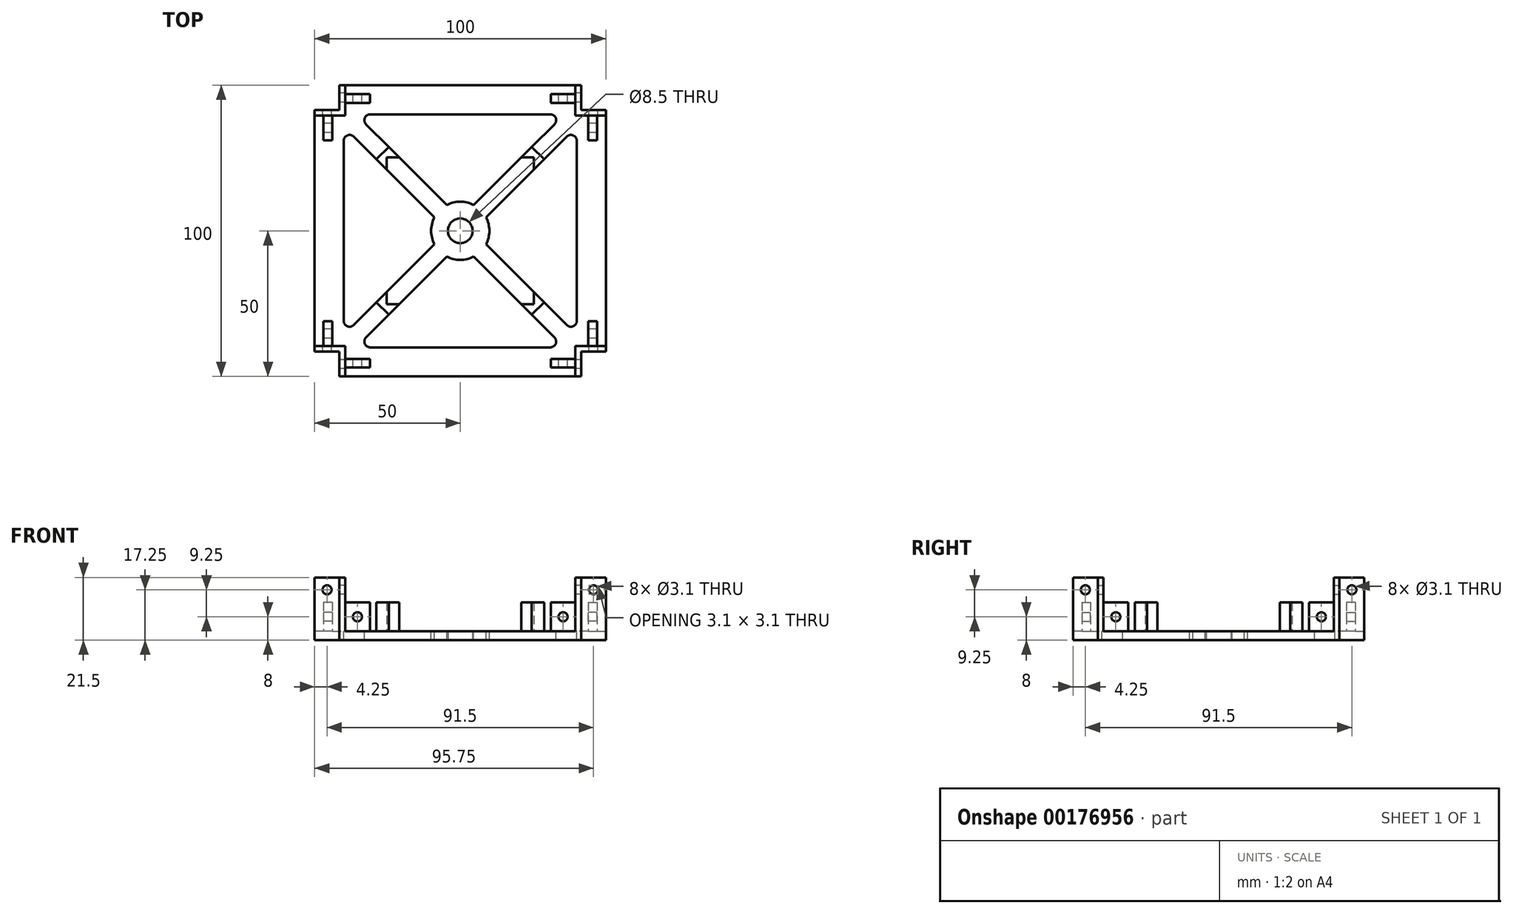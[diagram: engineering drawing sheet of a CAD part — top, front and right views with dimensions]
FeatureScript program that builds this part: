
annotation { "Feature Type Name" : "Feature", "Feature Type Description" : "" }
export const myFeature = defineFeature(function(context is Context, id is Id, definition is map)
    precondition{}
    {
        {
            assignVariable(context, id + "F0", {"name" : "thickness", "anyValue" : 3});
        }
        {
            var Q0;
            Q0=qCreatedBy(makeId("Top.planeOp"),FACE);
            var sketch = newSketch(context, id + "F1", { "sketchPlane" : qUnion([Q0])});
            skLineSegment(sketch, "E0.bottom", {"start": v(41.5, 50) * mm, "end": v(-41.5, 50) * mm});
            skLineSegment(sketch, "E0.top", {"start": v(41.5, -50) * mm, "end": v(-41.5, -50) * mm});
            skLineSegment(sketch, "E0.right", {"start": v(-50, 41.5) * mm, "end": v(-50, -41.5) * mm});
            skPoint(sketch, "E0.middle", {"position": v(0, 0) * mm});
            skLineSegment(sketch, "E1", {"start": v(-50, 41.5) * mm, "end": v(-41.5, 41.5) * mm});
            skLineSegment(sketch, "E2", {"start": v(-41.5, 41.5) * mm, "end": v(-41.5, 50) * mm});
            skLineSegment(sketch, "E3", {"start": v(0, 0) * mm, "end": v(0, 50) * mm, "construction": true});
            skLineSegment(sketch, "E4", {"start": v(0, 0) * mm, "end": v(50, 0) * mm, "construction": true});
            skLineSegment(sketch, "E5.MirrorCS", {"start": v(41.5, 41.5) * mm, "end": v(41.5, 50) * mm});
            skLineSegment(sketch, "E6.MirrorCS", {"start": v(50, 41.5) * mm, "end": v(41.5, 41.5) * mm});
            skLineSegment(sketch, "E7.MirrorCS", {"start": v(-50, -41.5) * mm, "end": v(-41.5, -41.5) * mm});
            skLineSegment(sketch, "E8.MirrorCS", {"start": v(-41.5, -41.5) * mm, "end": v(-41.5, -50) * mm});
            skLineSegment(sketch, "E9.MirrorCS", {"start": v(50, -41.5) * mm, "end": v(41.5, -41.5) * mm});
            skLineSegment(sketch, "E10.MirrorCS", {"start": v(50, -41.5) * mm, "end": v(50, 41.5) * mm});
            skLineSegment(sketch, "E11.MirrorCS", {"start": v(41.5, -41.5) * mm, "end": v(41.5, -50) * mm});
            skCircle(sketch, "E12", {"center": v(0, 0) * mm, "radius": 4.25 * mm});
            skSolve(sketch);
        }
        {
            var Q0;
            Q0=makeQuery(id+"F1.imprint","IMPRINT",FACE,{"disambiguationData":[TD([[makeQuery(id+"F1.imprint","IMPRINT",EDGE,{"derivedFrom":sQuery(id+"F1.wireOp",EDGE,"E0.bottom")}),1.0]])]});
            extrude(context, id + "F2", {"entities" : qUnion([Q0]), "depth" : (getVariable(context, 'thickness')) * mm});
        }
        {
            var Q0;
            Q0=makeQuery(id+"F2.opExtrude","CAP_FACE",FACE,{"disambiguationData":[OSD([sQuery(id+"F1.wireOp",EDGE,"E0.bottom"),sQuery(id+"F1.wireOp",EDGE,"E0.right"),sQuery(id+"F1.wireOp",EDGE,"E1"),sQuery(id+"F1.wireOp",EDGE,"E2"),sQuery(id+"F1.wireOp",EDGE,"E5.MirrorCS"),sQuery(id+"F1.wireOp",EDGE,"E6.MirrorCS"),sQuery(id+"F1.wireOp",EDGE,"E7.MirrorCS"),sQuery(id+"F1.wireOp",EDGE,"E8.MirrorCS"),sQuery(id+"F1.wireOp",EDGE,"E9.MirrorCS"),sQuery(id+"F1.wireOp",EDGE,"E10.MirrorCS"),sQuery(id+"F1.wireOp",EDGE,"E11.MirrorCS"),sQuery(id+"F1.wireOp",EDGE,"E0.top"),sQuery(id+"F1.wireOp",EDGE,"E12")])],"isStart":false});
            var sketch = newSketch(context, id + "F3", { "sketchPlane" : qUnion([Q0])});
            skLineSegment(sketch, "E13", {"start": v(39.55, 43.95) * mm, "end": v(39.55, 39.55) * mm});
            skLineSegment(sketch, "E14", {"start": v(50, 41.5) * mm, "end": v(41.5, 41.5) * mm});
            skLineSegment(sketch, "E15", {"start": v(41.5, 41.5) * mm, "end": v(41.5, 50) * mm});
            skLineSegment(sketch, "E16", {"start": v(39.55, 46.95) * mm, "end": v(31.05, 46.95) * mm});
            skLineSegment(sketch, "E17", {"start": v(0, 0) * mm, "end": v(0, 50) * mm, "construction": true});
            skLineSegment(sketch, "E18", {"start": v(0, 0) * mm, "end": v(50, 0) * mm, "construction": true});
            skLineSegment(sketch, "E19", {"start": v(31.05, 46.95) * mm, "end": v(31.05, 43.95) * mm});
            skLineSegment(sketch, "E20", {"start": v(31.05, 43.95) * mm, "end": v(39.55, 43.95) * mm});
            skLineSegment(sketch, "E21.0", {"start": v(46.95, 39.55) * mm, "end": v(46.95, 31.05) * mm});
            skLineSegment(sketch, "E22", {"start": v(43.95, 31.05) * mm, "end": v(46.95, 31.05) * mm});
            skLineSegment(sketch, "E23.trimOffspring", {"start": v(46.95, 39.55) * mm, "end": v(50, 39.55) * mm});
            skLineSegment(sketch, "E24", {"start": v(39.55, 46.95) * mm, "end": v(39.55, 50) * mm});
            skLineSegment(sketch, "E25", {"start": v(39.55, 50) * mm, "end": v(41.5, 50) * mm});
            skLineSegment(sketch, "E26", {"start": v(43.95, 39.55) * mm, "end": v(39.55, 39.55) * mm});
            skLineSegment(sketch, "E27.trimOffspring", {"start": v(43.95, 39.55) * mm, "end": v(43.95, 31.05) * mm});
            skLineSegment(sketch, "E28", {"start": v(50, 41.5) * mm, "end": v(50, 39.55) * mm});
            skSolve(sketch);
        }
        {
            var Q0;
            Q0=qSketchRegion(id+"F3",true);
            extrude(context, id + "F4", {"entities" : qUnion([Q0]), "depth" : 10 * mm});
        }
        {
            var Q0;
            Q0=makeQuery(id+"F4.opExtrude","SWEPT_BODY",BODY,{"disambiguationData":[OSD([sQuery(id+"F3.wireOp",EDGE,"E13"),sQuery(id+"F3.wireOp",EDGE,"nKXGrhFW-WUnw-J8YZ-HHNa-CiBs2QdvG3Ug"),sQuery(id+"F3.wireOp",EDGE,"9BF3yCzr-lQTs-itfY-5ALy-uFZCs8Egl8vE"),sQuery(id+"F3.wireOp",EDGE,"E14"),sQuery(id+"F3.wireOp",EDGE,"E15"),sQuery(id+"F3.wireOp",EDGE,"E16")])]});
            var Q1;
            Q1=qCreatedBy(makeId("Right.planeOp"),FACE);
            mirror(context, id + "F5", {"entities" : qUnion([Q0]), "mirrorPlane" : qUnion([Q1])});
        }
        {
            var Q0;
            Q0=makeQuery(id+"F5.opPattern","COPY",BODY,{"derivedFrom":makeQuery(id+"F4.opExtrude","SWEPT_BODY",BODY,{"disambiguationData":[OSD([sQuery(id+"F3.wireOp",EDGE,"E13"),sQuery(id+"F3.wireOp",EDGE,"nKXGrhFW-WUnw-J8YZ-HHNa-CiBs2QdvG3Ug"),sQuery(id+"F3.wireOp",EDGE,"9BF3yCzr-lQTs-itfY-5ALy-uFZCs8Egl8vE"),sQuery(id+"F3.wireOp",EDGE,"E14"),sQuery(id+"F3.wireOp",EDGE,"E15"),sQuery(id+"F3.wireOp",EDGE,"E16")])]}),"instanceName":"1"});
            var Q1;
            Q1=makeQuery(id+"F4.opExtrude","SWEPT_BODY",BODY,{"disambiguationData":[OSD([sQuery(id+"F3.wireOp",EDGE,"E13"),sQuery(id+"F3.wireOp",EDGE,"nKXGrhFW-WUnw-J8YZ-HHNa-CiBs2QdvG3Ug"),sQuery(id+"F3.wireOp",EDGE,"9BF3yCzr-lQTs-itfY-5ALy-uFZCs8Egl8vE"),sQuery(id+"F3.wireOp",EDGE,"E14"),sQuery(id+"F3.wireOp",EDGE,"E15"),sQuery(id+"F3.wireOp",EDGE,"E16")])]});
            var Q2;
            Q2=qCreatedBy(makeId("Front.planeOp"),FACE);
            mirror(context, id + "F6", {"operationType" : NewBodyOperationType.ADD, "entities" : qUnion([Q0, Q1]), "mirrorPlane" : qUnion([Q2])});
        }
        {
            var Q0;
            Q0=makeQuery(id+"F2.opExtrude","CAP_FACE",FACE,{"disambiguationData":[OSD([sQuery(id+"F1.wireOp",EDGE,"E0.bottom"),sQuery(id+"F1.wireOp",EDGE,"E0.right"),sQuery(id+"F1.wireOp",EDGE,"E1"),sQuery(id+"F1.wireOp",EDGE,"E2"),sQuery(id+"F1.wireOp",EDGE,"E5.MirrorCS"),sQuery(id+"F1.wireOp",EDGE,"E6.MirrorCS"),sQuery(id+"F1.wireOp",EDGE,"E7.MirrorCS"),sQuery(id+"F1.wireOp",EDGE,"E8.MirrorCS"),sQuery(id+"F1.wireOp",EDGE,"E9.MirrorCS"),sQuery(id+"F1.wireOp",EDGE,"E10.MirrorCS"),sQuery(id+"F1.wireOp",EDGE,"E11.MirrorCS"),sQuery(id+"F1.wireOp",EDGE,"E0.top"),sQuery(id+"F1.wireOp",EDGE,"E12")])],"isStart":false});
            var sketch = newSketch(context, id + "F7", { "sketchPlane" : qUnion([Q0])});
            skLineSegment(sketch, "E29.bottom", {"start": v(-30.93, 40) * mm, "end": v(30.93, 40) * mm});
            skLineSegment(sketch, "E29.top", {"start": v(-30.93, -40) * mm, "end": v(30.93, -40) * mm});
            skLineSegment(sketch, "E29.left", {"start": v(-40, 30.93) * mm, "end": v(-40, -30.93) * mm});
            skLineSegment(sketch, "E29.right", {"start": v(40, 30.93) * mm, "end": v(40, -30.93) * mm});
            skPoint(sketch, "E29.middle", {"position": v(0, 0) * mm});
            skLineSegment(sketch, "E30", {"start": v(-40, -40) * mm, "end": v(40, 40) * mm, "construction": true});
            skLineSegment(sketch, "E31.0", {"start": v(-32.34, -36.59) * mm, "end": v(-4.62, -8.87) * mm});
            skLineSegment(sketch, "E32.0", {"start": v(-36.59, -32.34) * mm, "end": v(-8.87, -4.62) * mm});
            skArc(sketch, "E33", {"start": v(-4.62, -8.87) * mm, "mid": v(0, -10) * mm, "end": v(4.62, -8.87) * mm});
            skLineSegment(sketch, "E34.trimOffspring", {"start": v(8.87, 4.62) * mm, "end": v(36.59, 32.34) * mm});
            skLineSegment(sketch, "E35.trimOffspring", {"start": v(4.62, 8.87) * mm, "end": v(32.34, 36.59) * mm});
            skArc(sketch, "E36.trimOffspring", {"start": v(4.62, 8.87) * mm, "mid": v(0, 10) * mm, "end": v(-4.62, 8.87) * mm});
            skLineSegment(sketch, "E37.MirrorCS", {"start": v(32.34, -36.59) * mm, "end": v(4.62, -8.87) * mm});
            skLineSegment(sketch, "E38.MirrorCS", {"start": v(36.59, -32.34) * mm, "end": v(8.87, -4.62) * mm});
            skLineSegment(sketch, "E39.MirrorCS", {"start": v(-8.87, 4.62) * mm, "end": v(-36.59, 32.34) * mm});
            skLineSegment(sketch, "E40.MirrorCS", {"start": v(-4.62, 8.87) * mm, "end": v(-32.34, 36.59) * mm});
            skArc(sketch, "E41.trimOffspring", {"start": v(8.87, -4.62) * mm, "mid": v(10, 0) * mm, "end": v(8.87, 4.62) * mm});
            skArc(sketch, "E42.trimOffspring", {"start": v(-8.87, 4.62) * mm, "mid": v(-10, 0) * mm, "end": v(-8.87, -4.62) * mm});
            skPoint(sketch, "E43.visualSharp", {"position": v(-35.76, -40) * mm});
            skArc(sketch, "E43.filletArc", {"start": v(-32.34, -36.59) * mm, "mid": v(-32.78, -38.77) * mm, "end": v(-30.93, -40) * mm});
            skPoint(sketch, "E44.visualSharp", {"position": v(35.76, -40) * mm});
            skArc(sketch, "E44.filletArc", {"start": v(30.93, -40) * mm, "mid": v(32.78, -38.77) * mm, "end": v(32.34, -36.59) * mm});
            skPoint(sketch, "E45.visualSharp", {"position": v(40, -35.76) * mm});
            skArc(sketch, "E45.filletArc", {"start": v(36.59, -32.34) * mm, "mid": v(38.77, -32.78) * mm, "end": v(40, -30.93) * mm});
            skPoint(sketch, "E46.visualSharp", {"position": v(40, 35.76) * mm});
            skArc(sketch, "E46.filletArc", {"start": v(40, 30.93) * mm, "mid": v(38.77, 32.78) * mm, "end": v(36.59, 32.34) * mm});
            skPoint(sketch, "E47.visualSharp", {"position": v(35.76, 40) * mm});
            skArc(sketch, "E47.filletArc", {"start": v(32.34, 36.59) * mm, "mid": v(32.78, 38.77) * mm, "end": v(30.93, 40) * mm});
            skPoint(sketch, "E48.visualSharp", {"position": v(-35.76, 40) * mm});
            skArc(sketch, "E48.filletArc", {"start": v(-30.93, 40) * mm, "mid": v(-32.78, 38.77) * mm, "end": v(-32.34, 36.59) * mm});
            skPoint(sketch, "E49.visualSharp", {"position": v(-40, 35.76) * mm});
            skArc(sketch, "E49.filletArc", {"start": v(-36.59, 32.34) * mm, "mid": v(-38.77, 32.78) * mm, "end": v(-40, 30.93) * mm});
            skPoint(sketch, "E50.visualSharp", {"position": v(-40, -35.76) * mm});
            skArc(sketch, "E50.filletArc", {"start": v(-40, -30.93) * mm, "mid": v(-38.77, -32.78) * mm, "end": v(-36.59, -32.34) * mm});
            skSolve(sketch);
        }
        {
            var Q0;
            Q0=makeQuery(id+"F7.imprint","IMPRINT",FACE,{"disambiguationData":[TD([[makeQuery(id+"F7.imprint","IMPRINT",EDGE,{"derivedFrom":sQuery(id+"F7.wireOp",EDGE,"E29.left")}),1.0]])]});
            var Q1;
            Q1=makeQuery(id+"F7.imprint","IMPRINT",FACE,{"disambiguationData":[TD([[makeQuery(id+"F7.imprint","IMPRINT",EDGE,{"derivedFrom":sQuery(id+"F7.wireOp",EDGE,"E29.bottom")}),-1.0]])]});
            var Q2;
            Q2=makeQuery(id+"F7.imprint","IMPRINT",FACE,{"disambiguationData":[TD([[makeQuery(id+"F7.imprint","IMPRINT",EDGE,{"derivedFrom":sQuery(id+"F7.wireOp",EDGE,"E29.right")}),-1.0]])]});
            var Q3;
            Q3=makeQuery(id+"F7.imprint","IMPRINT",FACE,{"disambiguationData":[TD([[makeQuery(id+"F7.imprint","IMPRINT",EDGE,{"derivedFrom":sQuery(id+"F7.wireOp",EDGE,"E29.top")}),1.0]])]});
            extrude(context, id + "F8", {"entities" : qUnion([Q0, Q1, Q2, Q3]), "operationType" : NewBodyOperationType.REMOVE, "endBound" : BoundingType.THROUGH_ALL, "oppositeDirection" : true, "depth" : 25 * mm});
        }
        {
            var Q0;
            Q0=makeQuery(id+"F4.opExtrude","CAP_FACE",FACE,{"disambiguationData":[OSD([sQuery(id+"F3.wireOp",EDGE,"E13"),sQuery(id+"F3.wireOp",EDGE,"E14"),sQuery(id+"F3.wireOp",EDGE,"E15"),sQuery(id+"F3.wireOp",EDGE,"E16"),sQuery(id+"F3.wireOp",EDGE,"E19"),sQuery(id+"F3.wireOp",EDGE,"E20"),sQuery(id+"F3.wireOp",EDGE,"E21.0"),sQuery(id+"F3.wireOp",EDGE,"E22"),sQuery(id+"F3.wireOp",EDGE,"E23.trimOffspring"),sQuery(id+"F3.wireOp",EDGE,"E24"),sQuery(id+"F3.wireOp",EDGE,"E25"),sQuery(id+"F3.wireOp",EDGE,"E26"),sQuery(id+"F3.wireOp",EDGE,"E27.trimOffspring"),sQuery(id+"F3.wireOp",EDGE,"E28")])],"isStart":false});
            var sketch = newSketch(context, id + "F9", { "sketchPlane" : qUnion([Q0])});
            skLineSegment(sketch, "E51", {"start": v(0, 0) * mm, "end": v(0, 50) * mm, "construction": true});
            skLineSegment(sketch, "E52", {"start": v(0, 0) * mm, "end": v(55.04, 0) * mm, "construction": true});
            skLineSegment(sketch, "E53.MirrorCS", {"start": v(39.55, 50) * mm, "end": v(41.5, 50) * mm});
            skLineSegment(sketch, "E54", {"start": v(50, 41.5) * mm, "end": v(50, 39.55) * mm});
            skLineSegment(sketch, "E55", {"start": v(39.55, 50) * mm, "end": v(39.55, 39.55) * mm});
            skLineSegment(sketch, "E56", {"start": v(39.55, 39.55) * mm, "end": v(50, 39.55) * mm});
            skLineSegment(sketch, "E57", {"start": v(41.5, 50) * mm, "end": v(41.5, 41.5) * mm});
            skLineSegment(sketch, "E58", {"start": v(41.5, 41.5) * mm, "end": v(50, 41.5) * mm});
            skLineSegment(sketch, "E59.MirrorCS", {"start": v(-50, 41.5) * mm, "end": v(-50, 39.55) * mm});
            skLineSegment(sketch, "E60.MirrorCS", {"start": v(-39.55, 50) * mm, "end": v(-41.5, 50) * mm});
            skLineSegment(sketch, "E61.MirrorCS", {"start": v(-41.5, 41.5) * mm, "end": v(-50, 41.5) * mm});
            skLineSegment(sketch, "E62.MirrorCS", {"start": v(-39.55, 50) * mm, "end": v(-39.55, 39.55) * mm});
            skLineSegment(sketch, "E63.MirrorCS", {"start": v(-39.55, 39.55) * mm, "end": v(-50, 39.55) * mm});
            skLineSegment(sketch, "E64.MirrorCS", {"start": v(-41.5, 50) * mm, "end": v(-41.5, 41.5) * mm});
            skLineSegment(sketch, "E65.MirrorCS", {"start": v(39.55, -50) * mm, "end": v(41.5, -50) * mm});
            skLineSegment(sketch, "E66.MirrorCS", {"start": v(-39.55, -50) * mm, "end": v(-41.5, -50) * mm});
            skLineSegment(sketch, "E67.MirrorCS", {"start": v(50, -41.5) * mm, "end": v(50, -39.55) * mm});
            skLineSegment(sketch, "E68.MirrorCS", {"start": v(-50, -41.5) * mm, "end": v(-50, -39.55) * mm});
            skLineSegment(sketch, "E69.MirrorCS", {"start": v(41.5, -50) * mm, "end": v(41.5, -41.5) * mm});
            skLineSegment(sketch, "E70.MirrorCS", {"start": v(41.5, -41.5) * mm, "end": v(50, -41.5) * mm});
            skLineSegment(sketch, "E71.MirrorCS", {"start": v(-41.5, -41.5) * mm, "end": v(-50, -41.5) * mm});
            skLineSegment(sketch, "E72.MirrorCS", {"start": v(39.55, -39.55) * mm, "end": v(50, -39.55) * mm});
            skLineSegment(sketch, "E73.MirrorCS", {"start": v(39.55, -50) * mm, "end": v(39.55, -39.55) * mm});
            skLineSegment(sketch, "E74.MirrorCS", {"start": v(-39.55, -39.55) * mm, "end": v(-50, -39.55) * mm});
            skLineSegment(sketch, "E75.MirrorCS", {"start": v(-41.5, -50) * mm, "end": v(-41.5, -41.5) * mm});
            skLineSegment(sketch, "E76.MirrorCS", {"start": v(-39.55, -50) * mm, "end": v(-39.55, -39.55) * mm});
            skSolve(sketch);
        }
        {
            var Q0;
            Q0=qSketchRegion(id+"F9",true);
            extrude(context, id + "F10", {"entities" : qUnion([Q0]), "operationType" : NewBodyOperationType.ADD, "depth" : 8.5 * mm});
        }
        {
            var Q0;
            Q0=makeQuery(id+"F10.boolean.opBoolean","MERGE",FACE,{"derivedFrom":[makeQuery(id+"F6.boolean.opBoolean","MERGE",FACE,{"derivedFrom":[makeQuery(id+"F2.opExtrude","SWEPT_FACE",FACE,{"disambiguationData":[OSD([sQuery(id+"F1.wireOp",EDGE,"E8.MirrorCS")])]}),makeQuery(id+"F6.opPattern","COPY",FACE,{"derivedFrom":makeQuery(id+"F5.opPattern","COPY",FACE,{"derivedFrom":makeQuery(id+"F4.opExtrude","SWEPT_FACE",FACE,{"disambiguationData":[OSD([sQuery(id+"F3.wireOp",EDGE,"E15")])]}),"instanceName":"1"}),"instanceName":"1"})]}),makeQuery(id+"F10.opExtrude","SWEPT_FACE",FACE,{"disambiguationData":[OSD([sQuery(id+"F9.wireOp",EDGE,"E75.MirrorCS")])]})]});
            var sketch = newSketch(context, id + "F11", { "sketchPlane" : qUnion([Q0])});
            skCircle(sketch, "E77", {"center": v(45.75, 17.25) * mm, "radius": 1.55 * mm});
            skCircle(sketch, "E78.MirrorC", {"center": v(-45.75, 17.25) * mm, "radius": 1.55 * mm});
            skSolve(sketch);
        }
        {
            var Q0;
            Q0=qSketchRegion(id+"F11",true);
            extrude(context, id + "F12", {"entities" : qUnion([Q0]), "operationType" : NewBodyOperationType.REMOVE, "endBound" : BoundingType.THROUGH_ALL, "oppositeDirection" : true, "depth" : 25 * mm});
        }
        {
            var Q0;
            Q0=makeQuery(id+"F10.boolean.opBoolean","MERGE",FACE,{"derivedFrom":[makeQuery(id+"F6.boolean.opBoolean","MERGE",FACE,{"derivedFrom":[makeQuery(id+"F2.opExtrude","SWEPT_FACE",FACE,{"disambiguationData":[OSD([sQuery(id+"F1.wireOp",EDGE,"E1")])]}),makeQuery(id+"F5.opPattern","COPY",FACE,{"derivedFrom":makeQuery(id+"F4.opExtrude","SWEPT_FACE",FACE,{"disambiguationData":[OSD([sQuery(id+"F3.wireOp",EDGE,"E14")])]}),"instanceName":"1"})]}),makeQuery(id+"F10.opExtrude","SWEPT_FACE",FACE,{"disambiguationData":[OSD([sQuery(id+"F9.wireOp",EDGE,"E61.MirrorCS")])]})]});
            var sketch = newSketch(context, id + "F13", { "sketchPlane" : qUnion([Q0])});
            skCircle(sketch, "E79", {"center": v(45.75, 17.25) * mm, "radius": 1.55 * mm});
            skCircle(sketch, "E80.MirrorC", {"center": v(-45.75, 17.25) * mm, "radius": 1.55 * mm});
            skSolve(sketch);
        }
        {
            var Q0;
            Q0=qSketchRegion(id+"F13",true);
            extrude(context, id + "F14", {"entities" : qUnion([Q0]), "operationType" : NewBodyOperationType.REMOVE, "endBound" : BoundingType.THROUGH_ALL, "oppositeDirection" : true, "depth" : 25 * mm});
        }
        {
            var Q0;
            Q0=makeQuery(id+"F5.opPattern","COPY",FACE,{"derivedFrom":makeQuery(id+"F4.opExtrude","SWEPT_FACE",FACE,{"disambiguationData":[OSD([sQuery(id+"F3.wireOp",EDGE,"E21.0")])]}),"instanceName":"1"});
            var sketch = newSketch(context, id + "F15", { "sketchPlane" : qUnion([Q0])});
            skCircle(sketch, "E81", {"center": v(-35.3, 8) * mm, "radius": 1.55 * mm});
            skPoint(sketch, "E81.centerSnap0", {"position": v(-31.05, 8) * mm});
            skPoint(sketch, "E81.centerSnap1", {"position": v(-35.3, 13) * mm});
            skCircle(sketch, "E82.MirrorC", {"center": v(35.3, 8) * mm, "radius": 1.55 * mm});
            skSolve(sketch);
        }
        {
            var Q0;
            Q0=qSketchRegion(id+"F15",true);
            extrude(context, id + "F16", {"entities" : qUnion([Q0]), "operationType" : NewBodyOperationType.REMOVE, "endBound" : BoundingType.THROUGH_ALL, "oppositeDirection" : true, "depth" : 25 * mm});
        }
        {
            var Q0;
            Q0=makeQuery(id+"F4.opExtrude","SWEPT_FACE",FACE,{"disambiguationData":[OSD([sQuery(id+"F3.wireOp",EDGE,"E16")])]});
            var sketch = newSketch(context, id + "F17", { "sketchPlane" : qUnion([Q0])});
            skCircle(sketch, "E83", {"center": v(-35.3, 8) * mm, "radius": 1.55 * mm});
            skPoint(sketch, "E83.centerSnap0", {"position": v(-35.3, 13) * mm});
            skPoint(sketch, "E83.centerSnap1", {"position": v(-31.05, 8) * mm});
            skCircle(sketch, "E84.MirrorC", {"center": v(35.3, 8) * mm, "radius": 1.55 * mm});
            skSolve(sketch);
        }
        {
            var Q0;
            Q0=qSketchRegion(id+"F17",true);
            extrude(context, id + "F18", {"entities" : qUnion([Q0]), "operationType" : NewBodyOperationType.REMOVE, "endBound" : BoundingType.THROUGH_ALL, "oppositeDirection" : true, "depth" : 25 * mm});
        }
        {
            var Q0;
            Q0=makeQuery(id+"F2.opExtrude","CAP_FACE",FACE,{"disambiguationData":[OSD([sQuery(id+"F1.wireOp",EDGE,"E0.bottom"),sQuery(id+"F1.wireOp",EDGE,"E0.right"),sQuery(id+"F1.wireOp",EDGE,"E1"),sQuery(id+"F1.wireOp",EDGE,"E2"),sQuery(id+"F1.wireOp",EDGE,"E5.MirrorCS"),sQuery(id+"F1.wireOp",EDGE,"E6.MirrorCS"),sQuery(id+"F1.wireOp",EDGE,"E7.MirrorCS"),sQuery(id+"F1.wireOp",EDGE,"E8.MirrorCS"),sQuery(id+"F1.wireOp",EDGE,"E9.MirrorCS"),sQuery(id+"F1.wireOp",EDGE,"E10.MirrorCS"),sQuery(id+"F1.wireOp",EDGE,"E11.MirrorCS"),sQuery(id+"F1.wireOp",EDGE,"E0.top"),sQuery(id+"F1.wireOp",EDGE,"E12")])],"isStart":false});
            var sketch = newSketch(context, id + "F19", { "sketchPlane" : qUnion([Q0])});
            skLineSegment(sketch, "E85", {"start": v(-43.95, 35.3) * mm, "end": v(-35.3, 35.3) * mm, "construction": true});
            skPoint(sketch, "E85.endSnap0", {"position": v(-35.3, 43.95) * mm});
            skLineSegment(sketch, "E86", {"start": v(-35.3, 35.3) * mm, "end": v(-35.3, 43.95) * mm, "construction": true});
            skLineSegment(sketch, "E87.0", {"start": v(-33.8, 33.8) * mm, "end": v(-33.8, 43.95) * mm, "construction": true});
            skLineSegment(sketch, "E88.0", {"start": v(-36.8, 36.8) * mm, "end": v(-36.8, 43.95) * mm, "construction": true});
            skLineSegment(sketch, "E89.0", {"start": v(-43.95, 33.8) * mm, "end": v(-33.8, 33.8) * mm, "construction": true});
            skLineSegment(sketch, "E90.0", {"start": v(-43.95, 36.8) * mm, "end": v(-36.8, 36.8) * mm, "construction": true});
            skLineSegment(sketch, "E91", {"start": v(-33.8, 33.8) * mm, "end": v(-33.8, 0) * mm, "construction": true});
            skLineSegment(sketch, "E92.MirrorCS", {"start": v(-33.8, -33.8) * mm, "end": v(-33.8, 0) * mm, "construction": true});
            skLineSegment(sketch, "E93.MirrorCS", {"start": v(33.8, -33.8) * mm, "end": v(33.8, 0) * mm, "construction": true});
            skLineSegment(sketch, "E94.MirrorCS", {"start": v(33.8, 33.8) * mm, "end": v(33.8, 0) * mm, "construction": true});
            skLineSegment(sketch, "E95", {"start": v(-33.8, 33.8) * mm, "end": v(33.8, 33.8) * mm, "construction": true});
            skLineSegment(sketch, "E96", {"start": v(-33.8, -33.8) * mm, "end": v(33.8, -33.8) * mm, "construction": true});
            skLineSegment(sketch, "E97.bottom", {"start": v(-25.25, 25.25) * mm, "end": v(25.25, 25.25) * mm, "construction": true});
            skLineSegment(sketch, "E97.top", {"start": v(-25.25, -25.25) * mm, "end": v(25.25, -25.25) * mm, "construction": true});
            skLineSegment(sketch, "E97.left", {"start": v(-25.25, 25.25) * mm, "end": v(-25.25, -25.25) * mm, "construction": true});
            skLineSegment(sketch, "E97.right", {"start": v(25.25, 25.25) * mm, "end": v(25.25, -25.25) * mm, "construction": true});
            skPoint(sketch, "E97.middle", {"position": v(0, 0) * mm});
            skLineSegment(sketch, "E98", {"start": v(-25.25, -25.25) * mm, "end": v(25.25, 25.25) * mm, "construction": true});
            skLineSegment(sketch, "E99", {"start": v(-25.25, 25.25) * mm, "end": v(25.25, -25.25) * mm, "construction": true});
            skLineSegment(sketch, "E100", {"start": v(25.25, 25.25) * mm, "end": v(21, 25.25) * mm});
            skLineSegment(sketch, "E101", {"start": v(21, 25.25) * mm, "end": v(24.54, 28.79) * mm});
            skLineSegment(sketch, "E102", {"start": v(25.25, 25.25) * mm, "end": v(25.25, 21) * mm});
            skLineSegment(sketch, "E103", {"start": v(24.54, 28.79) * mm, "end": v(28.79, 24.54) * mm});
            skLineSegment(sketch, "E104", {"start": v(25.25, 21) * mm, "end": v(28.79, 24.54) * mm});
            skLineSegment(sketch, "E105.MirrorCS", {"start": v(-25.25, 25.25) * mm, "end": v(-25.25, 21) * mm});
            skLineSegment(sketch, "E106.MirrorCS", {"start": v(-21, 25.25) * mm, "end": v(-24.54, 28.79) * mm});
            skLineSegment(sketch, "E107.MirrorCS", {"start": v(-24.54, 28.79) * mm, "end": v(-28.79, 24.54) * mm});
            skLineSegment(sketch, "E108.MirrorCS", {"start": v(-25.25, 21) * mm, "end": v(-28.79, 24.54) * mm});
            skLineSegment(sketch, "E109.MirrorCS", {"start": v(-25.25, 25.25) * mm, "end": v(-21, 25.25) * mm});
            skLineSegment(sketch, "E110.MirrorCS", {"start": v(-25.25, -25.25) * mm, "end": v(-21, -25.25) * mm});
            skLineSegment(sketch, "E111.MirrorCS", {"start": v(25.25, -25.25) * mm, "end": v(21, -25.25) * mm});
            skLineSegment(sketch, "E112.MirrorCS", {"start": v(-21, -25.25) * mm, "end": v(-24.54, -28.79) * mm});
            skLineSegment(sketch, "E113.MirrorCS", {"start": v(25.25, -21) * mm, "end": v(28.79, -24.54) * mm});
            skLineSegment(sketch, "E114.MirrorCS", {"start": v(-24.54, -28.79) * mm, "end": v(-28.79, -24.54) * mm});
            skLineSegment(sketch, "E115.MirrorCS", {"start": v(24.54, -28.79) * mm, "end": v(28.79, -24.54) * mm});
            skLineSegment(sketch, "E116.MirrorCS", {"start": v(25.25, -25.25) * mm, "end": v(25.25, -21) * mm});
            skLineSegment(sketch, "E117.MirrorCS", {"start": v(-25.25, -21) * mm, "end": v(-28.79, -24.54) * mm});
            skLineSegment(sketch, "E118.MirrorCS", {"start": v(-25.25, -25.25) * mm, "end": v(-25.25, -21) * mm});
            skLineSegment(sketch, "E119.MirrorCS", {"start": v(21, -25.25) * mm, "end": v(24.54, -28.79) * mm});
            skSolve(sketch);
        }
        {
            var Q0;
            Q0=qSketchRegion(id+"F19",true);
            extrude(context, id + "F20", {"entities" : qUnion([Q0]), "operationType" : NewBodyOperationType.ADD, "depth" : 10 * mm});
        }
    });
